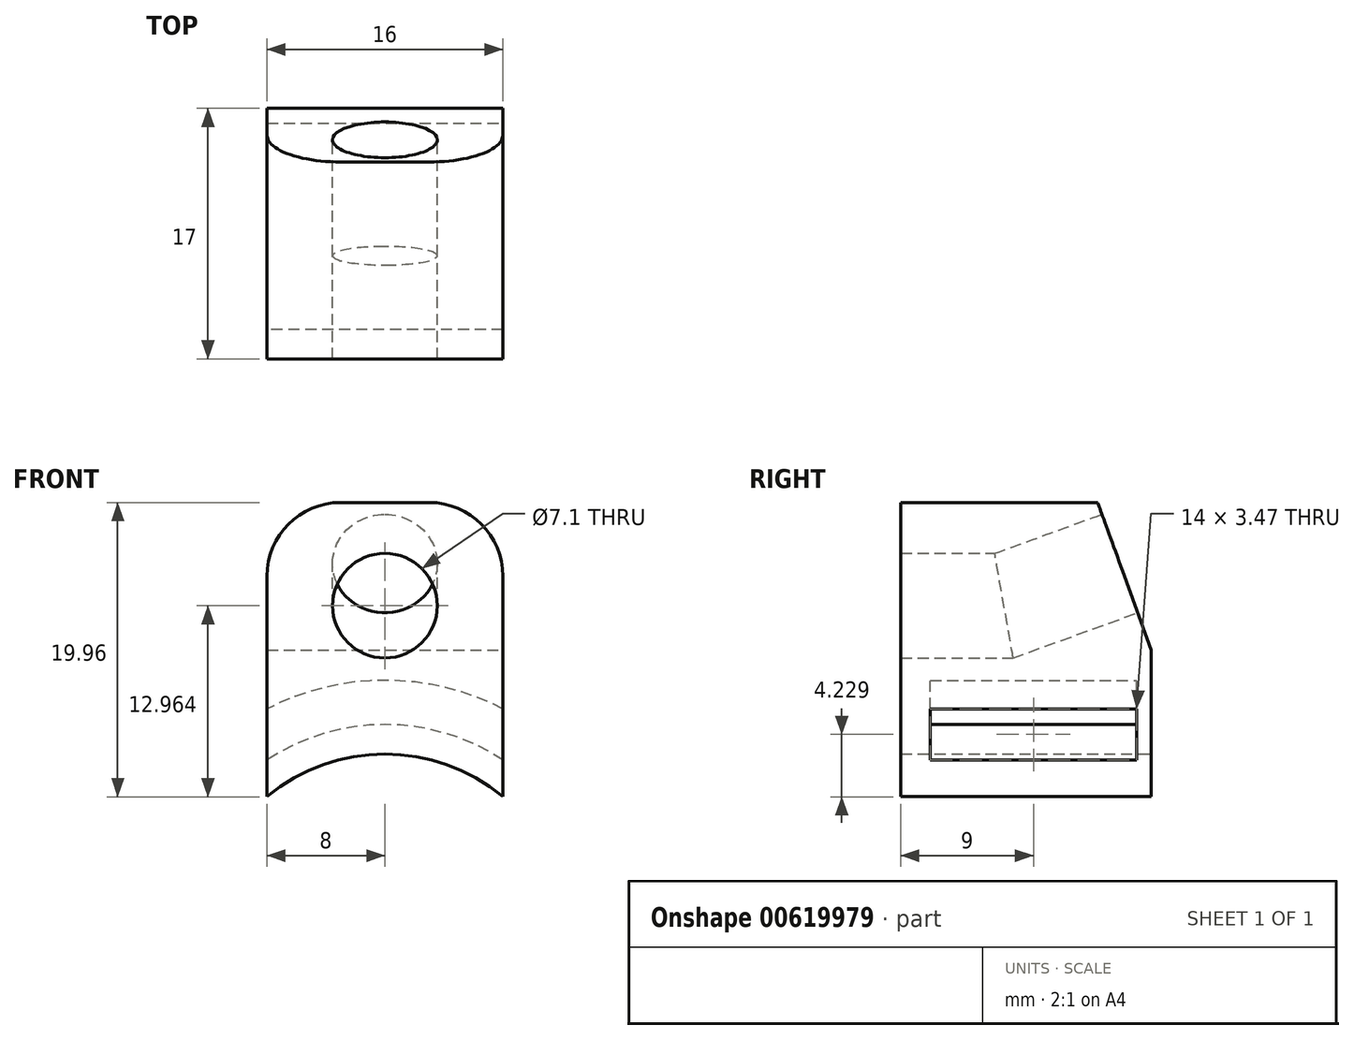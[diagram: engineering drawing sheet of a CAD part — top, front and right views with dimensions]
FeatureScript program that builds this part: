
annotation { "Feature Type Name" : "Feature", "Feature Type Description" : "" }
export const myFeature = defineFeature(function(context is Context, id is Id, definition is map)
    precondition{}
    {
        {
            var Q0;
            Q0=qCreatedBy(makeId("Front.planeOp"),FACE);
            var sketch = newSketch(context, id + "F0", { "sketchPlane" : qUnion([Q0])});
            skArc(sketch, "E0", {"start": v(8, 9.6) * mm, "mid": v(0, 12.5) * mm, "end": v(-8, 9.6) * mm});
            skArc(sketch, "E1.0", {"start": v(8, 12.1) * mm, "mid": v(0, 14.5) * mm, "end": v(-8, 12.1) * mm});
            skLineSegment(sketch, "E2", {"start": v(-8, 12.1) * mm, "end": v(-8, 9.6) * mm});
            skLineSegment(sketch, "E3", {"start": v(8, 12.1) * mm, "end": v(8, 9.6) * mm});
            skArc(sketch, "E4.0", {"start": v(8, 15.56) * mm, "mid": v(0, 17.5) * mm, "end": v(-8, 15.56) * mm});
            skLineSegment(sketch, "E5", {"start": v(-8, 15.56) * mm, "end": v(-8, 29.56) * mm});
            skLineSegment(sketch, "E6", {"start": v(8, 15.56) * mm, "end": v(8, 29.56) * mm});
            skLineSegment(sketch, "E7", {"start": v(8, 29.56) * mm, "end": v(-8, 29.56) * mm});
            skSolve(sketch);
        }
        {
            var Q0;
            Q0 = qSketchRegion(id + "F0", true);
            extrude(context, id + "F1", {"entities" : qUnion([Q0]), "depth" : 15 * mm, "offsetDistance" : 25 * mm});
        }
        {
            var Q0;
            Q0=makeQuery(id+"F1.opExtrude","CAP_FACE",FACE,{"disambiguationData":[OSD([sQuery(id+"F0.wireOp",EDGE,"E0"),sQuery(id+"F0.wireOp",EDGE,"E1.0"),sQuery(id+"F0.wireOp",EDGE,"E2"),sQuery(id+"F0.wireOp",EDGE,"E3")])],"isStart":false});
            var sketch = newSketch(context, id + "F2", { "sketchPlane" : qUnion([Q0])});
            skLineSegment(sketch, "E8.0", {"start": v(8, 9.6) * mm, "end": v(8, 12.1) * mm});
            skArc(sketch, "E8.1", {"start": v(-8, 9.6) * mm, "mid": v(0, 12.5) * mm, "end": v(8, 9.6) * mm});
            skLineSegment(sketch, "E8.2", {"start": v(-8, 12.1) * mm, "end": v(-8, 9.6) * mm});
            skArc(sketch, "E8.3", {"start": v(8, 12.1) * mm, "mid": v(0, 14.5) * mm, "end": v(-8, 12.1) * mm});
            skLineSegment(sketch, "E9.0", {"start": v(8, 15.56) * mm, "end": v(8, 29.56) * mm});
            skArc(sketch, "E9.1", {"start": v(-8, 15.56) * mm, "mid": v(0, 17.5) * mm, "end": v(8, 15.56) * mm});
            skLineSegment(sketch, "E9.2", {"start": v(-8, 29.56) * mm, "end": v(-8, 15.56) * mm});
            skLineSegment(sketch, "E9.3", {"start": v(8, 29.56) * mm, "end": v(-8, 29.56) * mm});
            skLineSegment(sketch, "E10", {"start": v(-8, 15.56) * mm, "end": v(-8, 12.1) * mm});
            skLineSegment(sketch, "E11", {"start": v(8, 15.56) * mm, "end": v(8, 12.1) * mm});
            skSolve(sketch);
        }
        {
            var Q0;
            Q0 = qSketchRegion(id + "F2", true);
            extrude(context, id + "F3", {"entities" : qUnion([Q0]), "depth" : 2 * mm, "offsetDistance" : 25 * mm});
        }
        {
            var Q0;
            Q0=makeQuery(id+"F1.opExtrude","SWEPT_FACE",FACE,{"disambiguationData":[OSD([sQuery(id+"F0.wireOp",EDGE,"E6")])]});
            var sketch = newSketch(context, id + "F4", { "sketchPlane" : qUnion([Q0])});
            skLineSegment(sketch, "E12", {"start": v(-16, 22.56) * mm, "end": v(-10, 22.56) * mm});
            skPoint(sketch, "E12.startSnap0", {"position": v(-14, 22.56) * mm});
            skLineSegment(sketch, "E13", {"start": v(-10, 22.56) * mm, "end": v(0, 26.2) * mm});
            skLineSegment(sketch, "E14", {"start": v(0, 26.2) * mm, "end": v(4.17, 27.72) * mm});
            skSolve(sketch);
        }
        {
            var Q0;
            Q0=makeQuery(id+"F3.opExtrude","CAP_FACE",FACE,{"disambiguationData":[OSD([sQuery(id+"F2.wireOp",EDGE,"E8.0"),sQuery(id+"F2.wireOp",EDGE,"E8.1"),sQuery(id+"F2.wireOp",EDGE,"E8.2"),sQuery(id+"F2.wireOp",EDGE,"E9.0"),sQuery(id+"F2.wireOp",EDGE,"E9.2"),sQuery(id+"F2.wireOp",EDGE,"E9.3"),sQuery(id+"F2.wireOp",EDGE,"E10"),sQuery(id+"F2.wireOp",EDGE,"E11"),sQuery(id+"F2.wireOp",EDGE,"e9b16d49-b053-4362-8564-5e08e6ca001d.0")])],"isStart":false});
            var sketch = newSketch(context, id + "F5", { "sketchPlane" : qUnion([Q0])});
            skCircle(sketch, "E15", {"center": v(0, 22.56) * mm, "radius": 3.55 * mm});
            skSolve(sketch);
        }
        {
            var Q0;
            Q0 = qSketchRegion(id + "F5", true);
            var Q1;
            Q1 = qConstructionFilter(qBodyType(qCreatedBy(id + "F4" ,EDGE), BodyType.WIRE), ConstructionObject.NO);
            sweep(context, id + "F6", {"operationType" : NewBodyOperationType.REMOVE, "profiles" : qUnion([Q0]), "path" : qUnion([Q1])});
        }
        {
            var Q0;
            Q0=makeQuery(id+"F1.opExtrude","SWEPT_FACE",FACE,{"disambiguationData":[OSD([sQuery(id+"F0.wireOp",EDGE,"E6")])]});
            var sketch = newSketch(context, id + "F7", { "sketchPlane" : qUnion([Q0])});
            skLineSegment(sketch, "E16", {"start": v(0, 19.56) * mm, "end": v(-3.64, 29.56) * mm});
            skLineSegment(sketch, "E17", {"start": v(-3.64, 29.56) * mm, "end": v(0, 29.56) * mm});
            skLineSegment(sketch, "E18", {"start": v(0, 29.56) * mm, "end": v(0, 19.56) * mm});
            skSolve(sketch);
        }
        {
            var Q0;
            Q0 = qSketchRegion(id + "F7", true);
            extrude(context, id + "F8", {"entities" : qUnion([Q0]), "operationType" : NewBodyOperationType.REMOVE, "oppositeDirection" : true, "depth" : 25 * mm, "offsetDistance" : 25 * mm});
        }
        {
            var Q0;
            Q0=makeQuery(id+"F1.opExtrude","SWEPT_BODY",BODY,{"disambiguationData":[OSD([sQuery(id+"F0.wireOp",EDGE,"E0"),sQuery(id+"F0.wireOp",EDGE,"E1.0"),sQuery(id+"F0.wireOp",EDGE,"E2"),sQuery(id+"F0.wireOp",EDGE,"E3")])]});
            var Q1;
            Q1=makeQuery(id+"F1.opExtrude","SWEPT_BODY",BODY,{"disambiguationData":[OSD([sQuery(id+"F0.wireOp",EDGE,"E4.0"),sQuery(id+"F0.wireOp",EDGE,"E5"),sQuery(id+"F0.wireOp",EDGE,"E6"),sQuery(id+"F0.wireOp",EDGE,"E7")])]});
            var Q2;
            Q2=makeQuery(id+"F3.opExtrude","SWEPT_BODY",BODY,{"disambiguationData":[OSD([sQuery(id+"F2.wireOp",EDGE,"E8.0"),sQuery(id+"F2.wireOp",EDGE,"E8.1"),sQuery(id+"F2.wireOp",EDGE,"E8.2"),sQuery(id+"F2.wireOp",EDGE,"E9.0"),sQuery(id+"F2.wireOp",EDGE,"E9.2"),sQuery(id+"F2.wireOp",EDGE,"E9.3"),sQuery(id+"F2.wireOp",EDGE,"E10"),sQuery(id+"F2.wireOp",EDGE,"E11")])]});
            booleanBodies(context, id + "F9", {"operationType" : BooleanOperationType.UNION, "tools" : qUnion([Q0, Q1, Q2])});
        }
        {
            var Q0;
            Q0=makeQuery(id+"F1.opExtrude","CAP_FACE",FACE,{"disambiguationData":[OSD([sQuery(id+"F0.wireOp",EDGE,"E0"),sQuery(id+"F0.wireOp",EDGE,"E1.0"),sQuery(id+"F0.wireOp",EDGE,"E2"),sQuery(id+"F0.wireOp",EDGE,"E3")])],"isStart":true});
            var sketch = newSketch(context, id + "F10", { "sketchPlane" : qUnion([Q0])});
            skLineSegment(sketch, "E19.0", {"start": v(-8, 12.1) * mm, "end": v(-8, 9.6) * mm});
            skArc(sketch, "E19.1", {"start": v(8, 12.1) * mm, "mid": v(0, 14.5) * mm, "end": v(-8, 12.1) * mm});
            skLineSegment(sketch, "E19.2", {"start": v(8, 9.6) * mm, "end": v(8, 12.1) * mm});
            skArc(sketch, "E19.3", {"start": v(-8, 9.6) * mm, "mid": v(0, 12.5) * mm, "end": v(8, 9.6) * mm});
            skLineSegment(sketch, "E20.0", {"start": v(8, 15.56) * mm, "end": v(8, 19.56) * mm});
            skArc(sketch, "E20.1", {"start": v(-8, 15.56) * mm, "mid": v(0, 17.5) * mm, "end": v(8, 15.56) * mm});
            skLineSegment(sketch, "E20.2", {"start": v(-8, 19.56) * mm, "end": v(-8, 15.56) * mm});
            skLineSegment(sketch, "E20.3", {"start": v(8, 19.56) * mm, "end": v(-8, 19.56) * mm});
            skLineSegment(sketch, "E21", {"start": v(-8, 12.1) * mm, "end": v(-8, 15.56) * mm});
            skLineSegment(sketch, "E22", {"start": v(8, 15.56) * mm, "end": v(8, 12.1) * mm});
            skSolve(sketch);
        }
        {
            var Q0;
            Q0 = qSketchRegion(id + "F10", true);
            extrude(context, id + "F11", {"entities" : qUnion([Q0]), "operationType" : NewBodyOperationType.ADD, "oppositeDirection" : true, "depth" : 1 * mm, "offsetDistance" : 25 * mm});
        }
        {
            var Q0;
            Q0=makeQuery(id+"F9.opBoolean","MERGE",EDGE,{"derivedFrom":[makeQuery(id+"F3.opExtrude","SWEPT_EDGE",EDGE,{"disambiguationData":[OSD([sQuery(id+"F2.wireOp",EDGE,"E9.0"),sQuery(id+"F2.wireOp",EDGE,"E9.3")])]}),makeQuery(id+"F1.opExtrude","SWEPT_EDGE",EDGE,{"disambiguationData":[OSD([sQuery(id+"F0.wireOp",EDGE,"E6"),sQuery(id+"F0.wireOp",EDGE,"E7")])]})]});
            var Q1;
            Q1=makeQuery(id+"F9.opBoolean","MERGE",EDGE,{"derivedFrom":[makeQuery(id+"F3.opExtrude","SWEPT_EDGE",EDGE,{"disambiguationData":[OSD([sQuery(id+"F2.wireOp",EDGE,"E9.2"),sQuery(id+"F2.wireOp",EDGE,"E9.3")])]}),makeQuery(id+"F1.opExtrude","SWEPT_EDGE",EDGE,{"disambiguationData":[OSD([sQuery(id+"F0.wireOp",EDGE,"E5"),sQuery(id+"F0.wireOp",EDGE,"E7")])]})]});
            fillet(context, id + "F12", {"entities" : qUnion([Q0, Q1]), "radius" : 5 * mm, "tangentPropagation" : true, "allowEdgeOverflow" : false});
        }
    });
